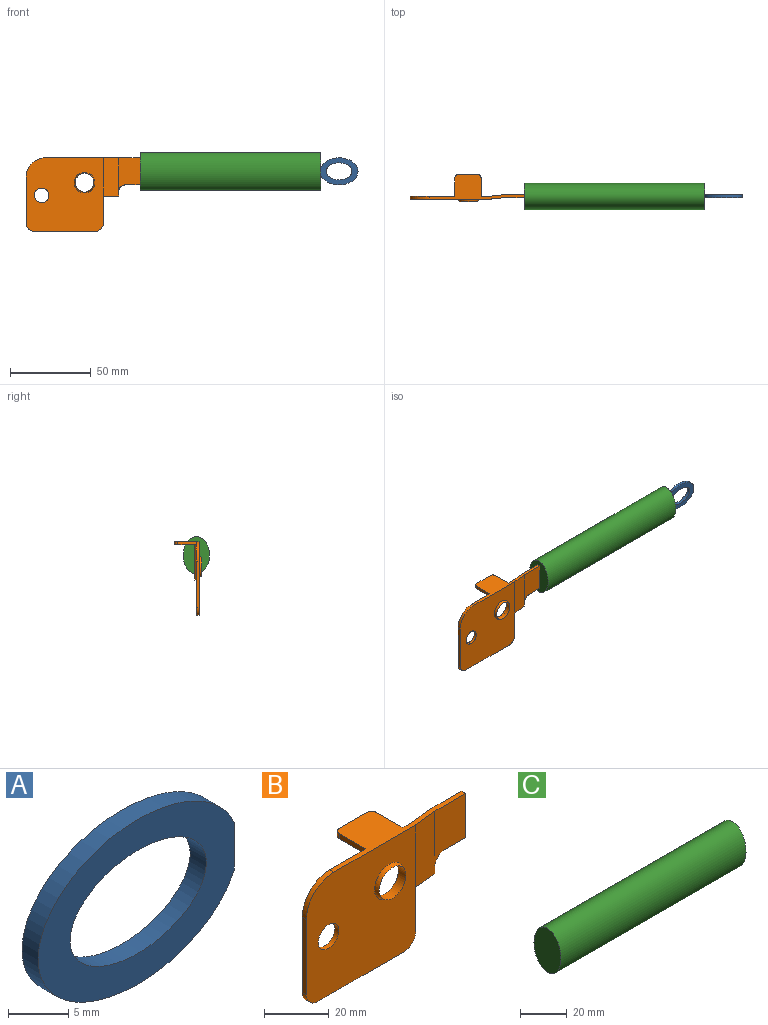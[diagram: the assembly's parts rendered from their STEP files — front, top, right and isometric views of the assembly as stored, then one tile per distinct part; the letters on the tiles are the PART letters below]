
ASSEMBLY  parts=3 mates=2
PART A: 5 faces, bbox 23x1.9x16.8 mm
  f0: plane 4.82x1.9mm, normal (1,0,0), area 9.1mm2, adj f2,f3,f4
  f1: extruded ~16x10.5mm, area 79.9mm2, adj f3,f4
  f2: extruded ~23x16.76mm, area 111.6mm2, adj f0,f3,f4
  f3: plane 23x16.77mm, normal (0,-1,0), area 175.9mm2, adj f0,f1,f2
  f4: plane 23x16.77mm, normal (0,1,0), area 175.9mm2, adj f0,f1,f2
PART B: 28 faces, bbox 70.8x16.9x45.5 mm
  f0: plane 16.83x1.8mm, normal (1,0,0), area 30.3mm2, adj f1,f7,f10,f20
  f1: plane 47.83x45.53mm, normal (0,1,0), area 1935.3mm2, adj f0,f2,f3,f4,f5,f6,f7,f8
  f2: plane 58.78x15.42mm, normal (0,0,1), area 324.5mm2, adj f1,f3,f10,f11,f12,f13,f15,f16
  f3: cylinder r=12mm len=12mm, axis (0,1,0), area 33.9mm2, adj f1,f2,f4,f10
  f4: plane 28.53x1.8mm, normal (-1,0,0), area 51.4mm2, adj f1,f3,f5,f10
  f5: cylinder r=5mm len=5mm, axis (0,1,0), area 14.1mm2, adj f1,f4,f6,f10
  f6: plane 37.83x1.8mm, normal (0,0,-1), area 68.1mm2, adj f1,f5,f7,f10
  f7: cylinder r=5mm len=5mm, axis (0,1,0), area 14.1mm2, adj f0,f1,f6,f10
  f8: cylinder r=4.5mm len=9mm, axis (0,1,0), area 50.9mm2, adj f1,f10
  f9: cylinder r=6.37mm len=12.74mm, axis (0,1,0), area 26.8mm2, adj f10,f27
  f10: plane 47.83x45.53mm, normal (0,-1,0), area 1945mm2, adj f0,f2,f3,f4,f5,f6,f7,f8
  f11: plane 11.5x1.9mm, normal (-1,0,0), area 21.9mm2, adj f1,f2,f14,f16
  f12: plane 11.5x1.9mm, normal (1,0,0), area 21.9mm2, adj f1,f2,f14,f15
  f13: plane 11.97x1.9mm, normal (0,1,0), area 22.7mm2, adj f2,f14,f15,f16
  f14: plane 16.2x13.62mm, normal (0,0,-1), area 218.7mm2, adj f1,f11,f12,f13,f15,f16
  f15: cylinder r=2.12mm len=2.12mm, axis (0,0,-1), area 6.3mm2, adj f2,f12,f13,f14
  f16: cylinder r=2.12mm len=2.12mm, axis (0,0,1), area 6.3mm2, adj f2,f11,f13,f14
  f17: plane 23.7x9.45mm, normal (0.11,-0.99,0), area 225.2mm2, adj f2,f10,f18,f20,f21
  f18: plane 2.66x1.8mm, normal (1,0,0), area 4.8mm2, adj f17,f19,f20,f25
  f19: plane 23.7x9.45mm, normal (-0.11,0.99,0), area 225.2mm2, adj f1,f2,f18,f20,f23
  f20: plane 9.45x2.8mm, normal (0,0,-1), area 17mm2, adj f0,f17,f18,f19
  f21: plane 21.04x13.5mm, normal (0,-1,0), area 230.7mm2, adj f2,f17,f22,f24,f25
  f22: plane 16.8x1.8mm, normal (1,0,0), area 30.2mm2, adj f2,f21,f23,f24
  f23: plane 21.04x13.5mm, normal (0,1,0), area 230.7mm2, adj f2,f19,f22,f24,f25
  f24: plane 9.26x1.8mm, normal (0,0,-1), area 16.7mm2, adj f21,f22,f23,f25
  f25: cylinder r=4.24mm len=4.24mm, axis (0,1,0), area 12mm2, adj f18,f21,f23,f24
  f26: cylinder r=5.82mm len=11.64mm, axis (0,1,0), area 120.7mm2, adj f1,f27
  f27: torus R=1.81mm, axis (0,-1,0), area 87.9mm2, adj f9,f26
PART C: 3 faces, bbox 111.8x16.3x23.1 mm
  f0: extruded ~111.8x23.13mm, area 6976.5mm2, adj f1,f2
  f1: plane 23.13x16.3mm, normal (1,0,0), area 296.1mm2, adj f0
  f2: plane 23.13x16.3mm, normal (-1,0,0), area 296.1mm2, adj f0
PLACE A rot(axis=(0,0,-1),180deg) t=(86.7,47.27,-63.24)mm
PLACE B rot(axis=(0,0,-1),0deg) t=(-2.21,48.12,-43.7)mm
PLACE C at identity
MATE fastened A.f0 <-> C.f1  axis (-1,0,0) through (111.8,48.22,-18.43)mm
MATE fastened B.f22 <-> C.f2  axis (1,0,0) through (0,48.22,-18.43)mm
